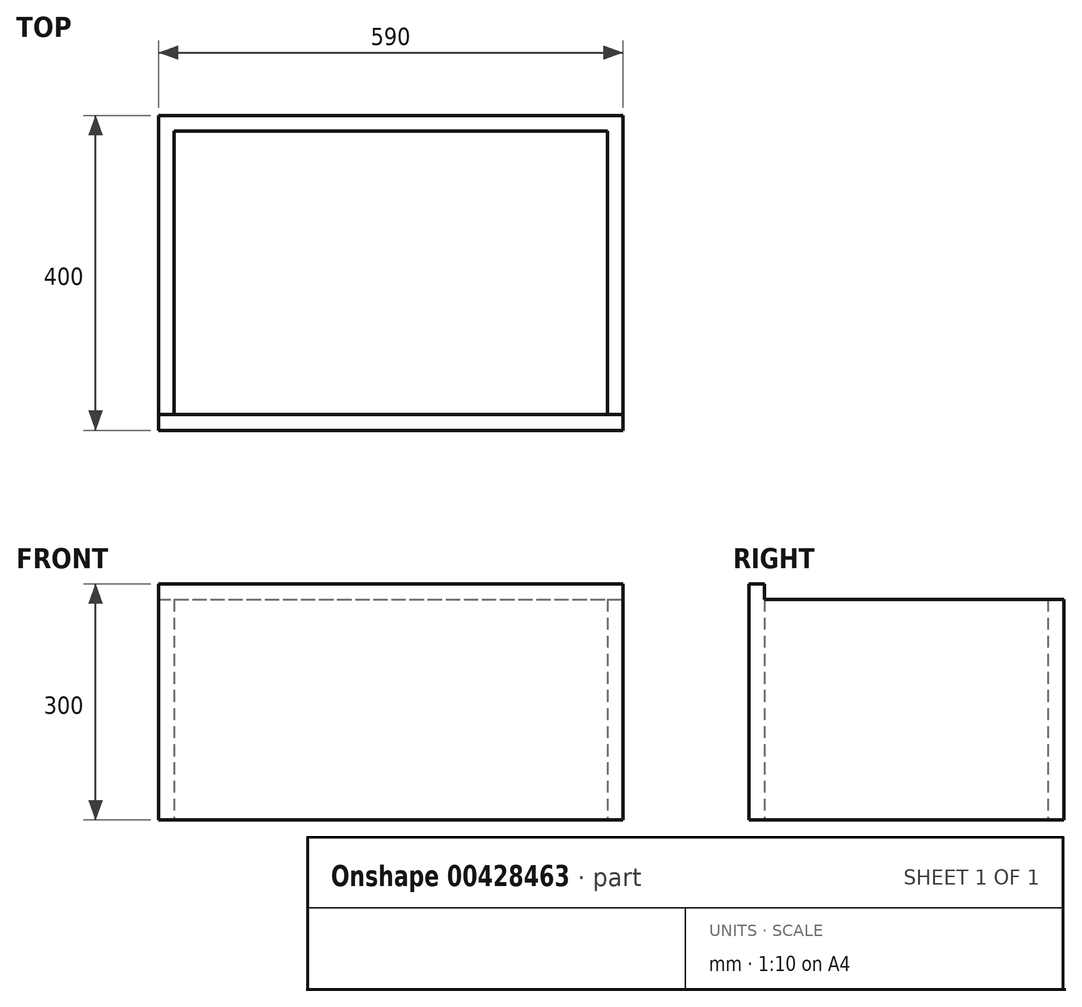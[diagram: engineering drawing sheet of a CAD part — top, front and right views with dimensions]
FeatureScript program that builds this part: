
annotation { "Feature Type Name" : "Feature", "Feature Type Description" : "" }
export const myFeature = defineFeature(function(context is Context, id is Id, definition is map)
    precondition{}
    {
        {
            var Q0;
            Q0=qCreatedBy(makeId("Top.planeOp"),FACE);
            var sketch = newSketch(context, id + "F0", { "sketchPlane" : qUnion([Q0])});
            skLineSegment(sketch, "E0.bottom", {"start": v(-295, 200) * mm, "end": v(295, 200) * mm});
            skLineSegment(sketch, "E0.top", {"start": v(-295, -200) * mm, "end": v(295, -200) * mm});
            skLineSegment(sketch, "E0.left", {"start": v(-295, 200) * mm, "end": v(-295, -200) * mm});
            skLineSegment(sketch, "E0.right", {"start": v(295, 200) * mm, "end": v(295, -200) * mm});
            skPoint(sketch, "E0.middle", {"position": v(0, 0) * mm});
            skLineSegment(sketch, "E1.0", {"start": v(-275, 200) * mm, "end": v(-275, -200) * mm});
            skLineSegment(sketch, "E2.0", {"start": v(-295, 180) * mm, "end": v(295, 180) * mm});
            skLineSegment(sketch, "E3.0", {"start": v(275, 200) * mm, "end": v(275, -200) * mm});
            skLineSegment(sketch, "E4.0", {"start": v(-295, -180) * mm, "end": v(295, -180) * mm});
            skSolve(sketch);
        }
        {
            var Q0;
            {var subQ0=sQuery(id+"F0.wireOp",EDGE,"E0.left");var subQ1=sQuery(id+"F0.wireOp",EDGE,"E0.bottom");var subQ2=makeQuery(id+"F0.imprint","INTERSECT",VERTEX,{"derivedFrom":[subQ1,subQ0]});Q0=makeQuery(id+"F0.imprint","IMPRINT",FACE,{"disambiguationData":[TD([[makeQuery(id+"F0.imprint","IMPRINT",EDGE,{"disambiguationData":[TD([[subQ2,-1.0]])],"derivedFrom":subQ1}),-1.0]])]});}
            var Q1;
            {var subQ0=sQuery(id+"F0.wireOp",EDGE,"E0.right");var subQ1=sQuery(id+"F0.wireOp",EDGE,"E0.bottom");var subQ2=makeQuery(id+"F0.imprint","INTERSECT",VERTEX,{"derivedFrom":[subQ1,subQ0]});Q1=makeQuery(id+"F0.imprint","IMPRINT",FACE,{"disambiguationData":[TD([[makeQuery(id+"F0.imprint","IMPRINT",EDGE,{"disambiguationData":[TD([[subQ2,1.0]])],"derivedFrom":subQ1}),-1.0]])]});}
            var Q2;
            {var subQ0=sQuery(id+"F0.wireOp",EDGE,"E1.0");var subQ1=sQuery(id+"F0.wireOp",EDGE,"E0.bottom");var subQ2=makeQuery(id+"F0.imprint","INTERSECT",VERTEX,{"derivedFrom":[subQ1,subQ0]});Q2=makeQuery(id+"F0.imprint","IMPRINT",FACE,{"disambiguationData":[TD([[makeQuery(id+"F0.imprint","IMPRINT",EDGE,{"disambiguationData":[TD([[subQ2,-1.0]])],"derivedFrom":subQ1}),-1.0]])]});}
            var Q3;
            {var subQ0=sQuery(id+"F0.wireOp",EDGE,"E2.0");var subQ1=sQuery(id+"F0.wireOp",EDGE,"E0.left");var subQ2=makeQuery(id+"F0.imprint","INTERSECT",VERTEX,{"derivedFrom":[subQ1,subQ0]});Q3=makeQuery(id+"F0.imprint","IMPRINT",FACE,{"disambiguationData":[TD([[makeQuery(id+"F0.imprint","IMPRINT",EDGE,{"disambiguationData":[TD([[subQ2,-1.0]])],"derivedFrom":subQ1}),1.0]])]});}
            var Q4;
            {var subQ0=sQuery(id+"F0.wireOp",EDGE,"E2.0");var subQ1=sQuery(id+"F0.wireOp",EDGE,"E0.right");var subQ2=makeQuery(id+"F0.imprint","INTERSECT",VERTEX,{"derivedFrom":[subQ1,subQ0]});Q4=makeQuery(id+"F0.imprint","IMPRINT",FACE,{"disambiguationData":[TD([[makeQuery(id+"F0.imprint","IMPRINT",EDGE,{"disambiguationData":[TD([[subQ2,-1.0]])],"derivedFrom":subQ1}),-1.0]])]});}
            extrude(context, id + "F1", {"entities" : qUnion([Q0, Q1, Q2, Q3, Q4]), "depth" : 280 * mm});
        }
        {
            var Q0;
            {var subQ0=sQuery(id+"F0.wireOp",EDGE,"E0.left");var subQ1=sQuery(id+"F0.wireOp",EDGE,"E0.top");var subQ2=makeQuery(id+"F0.imprint","INTERSECT",VERTEX,{"derivedFrom":[subQ1,subQ0]});Q0=makeQuery(id+"F0.imprint","IMPRINT",FACE,{"disambiguationData":[TD([[makeQuery(id+"F0.imprint","IMPRINT",EDGE,{"disambiguationData":[TD([[subQ2,-1.0]])],"derivedFrom":subQ1}),1.0]])]});}
            var Q1;
            {var subQ0=sQuery(id+"F0.wireOp",EDGE,"E1.0");var subQ1=sQuery(id+"F0.wireOp",EDGE,"E0.top");var subQ2=makeQuery(id+"F0.imprint","INTERSECT",VERTEX,{"derivedFrom":[subQ1,subQ0]});Q1=makeQuery(id+"F0.imprint","IMPRINT",FACE,{"disambiguationData":[TD([[makeQuery(id+"F0.imprint","IMPRINT",EDGE,{"disambiguationData":[TD([[subQ2,-1.0]])],"derivedFrom":subQ1}),1.0]])]});}
            var Q2;
            {var subQ0=sQuery(id+"F0.wireOp",EDGE,"E0.right");var subQ1=sQuery(id+"F0.wireOp",EDGE,"E0.top");var subQ2=makeQuery(id+"F0.imprint","INTERSECT",VERTEX,{"derivedFrom":[subQ1,subQ0]});Q2=makeQuery(id+"F0.imprint","IMPRINT",FACE,{"disambiguationData":[TD([[makeQuery(id+"F0.imprint","IMPRINT",EDGE,{"disambiguationData":[TD([[subQ2,1.0]])],"derivedFrom":subQ1}),1.0]])]});}
            extrude(context, id + "F2", {"entities" : qUnion([Q0, Q1, Q2]), "operationType" : NewBodyOperationType.ADD, "depth" : 300 * mm});
        }
    });
